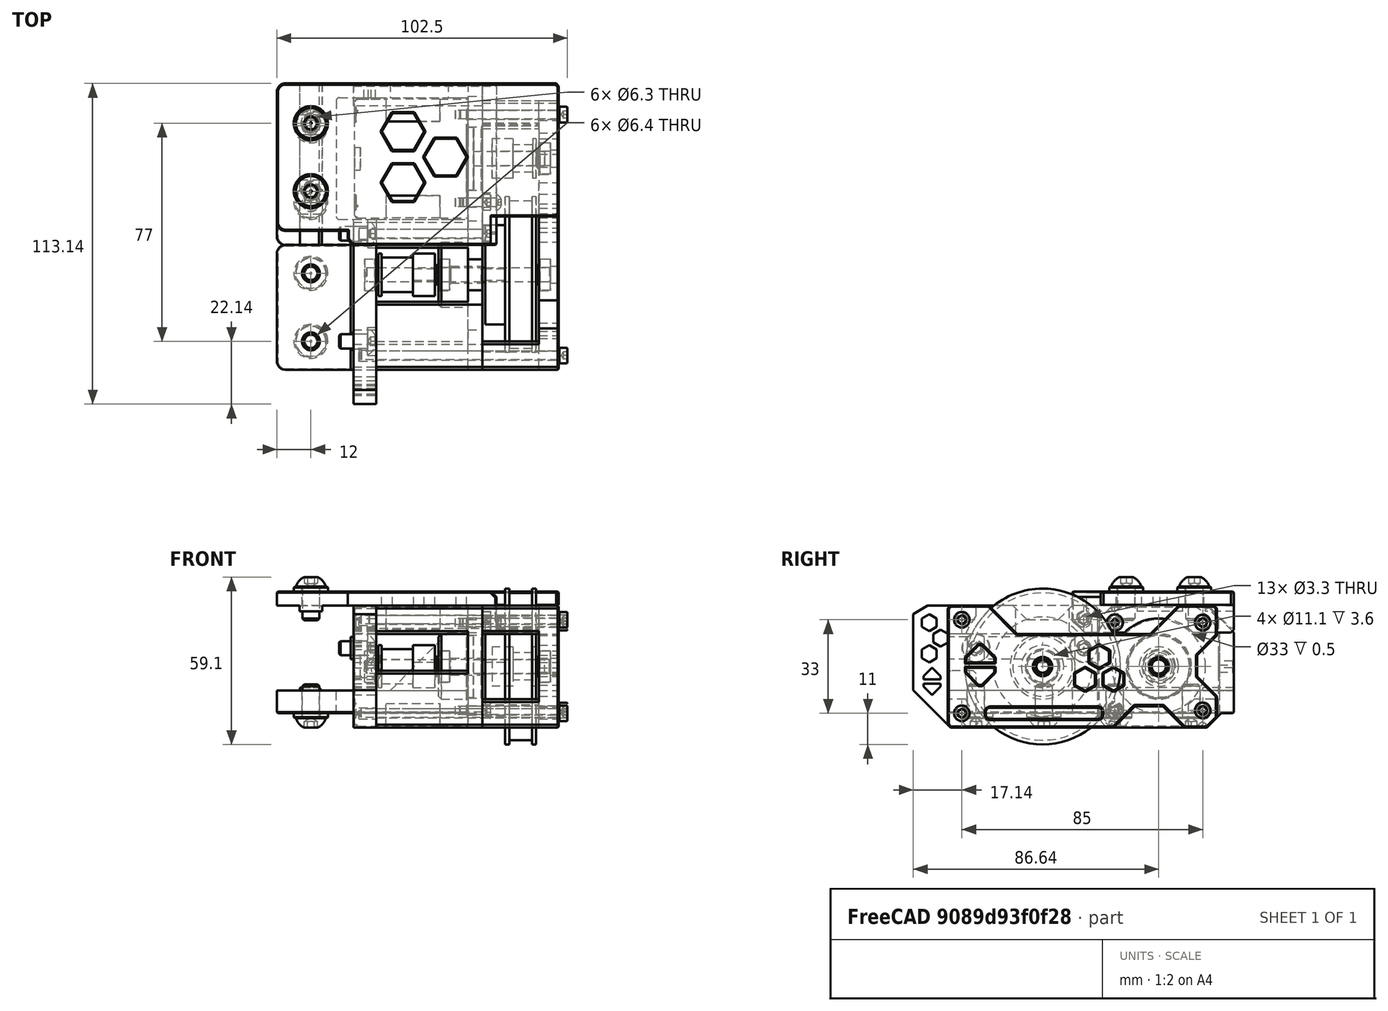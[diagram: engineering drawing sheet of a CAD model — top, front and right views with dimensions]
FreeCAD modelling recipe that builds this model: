
FCSTD DOCUMENT  (FreeCAD 0.19R24291 (Git))
Label: z-motor-left-assembly
License: Other
LicenseURL: GPL3
objects: Part::FeaturePython×21, Part::Feature×16, App::Part×1
note: 37 computed .brp shape members not serialized (recipe doc carries the construction recipe); baked Part::Feature solids carry a one-line shape summary decoded from their .brp

FEATURE [Part::Feature] Part__Mirroring014002  label="5mm-washer005"
  shape: bbox 0.5 x 6.9 x 6.9 mm, 4 faces (baked)
FEATURE [Part::Feature] Part__Mirroring002001  label="MR115ZZ006"
  shape: bbox 4 x 11 x 11 mm, 4 faces (baked)
FEATURE [Part::Feature] Part__Mirroring004001  label="20t-pulley001"
  shape: bbox 20 x 15 x 15 mm, 8 faces (baked)
FEATURE [Part::Feature] Part__Mirroring005001  label="MR115ZZ005"
  shape: bbox 4 x 11 x 11 mm, 4 faces (baked)
FEATURE [Part::Feature] Part__Mirroring007001  label="5mm-washer008"
  shape: bbox 0.5 x 6.9 x 6.9 mm, 4 faces (baked)
FEATURE [Part::Feature] Part__Mirroring008001  label="MR115ZZ007"
  shape: bbox 4 x 11 x 11 mm, 4 faces (baked)
FEATURE [Part::Feature] Part__Mirroring009001  label="motor-40mm001"
  shape: bbox 67 x 47 x 42 mm, 100 faces (baked)
FEATURE [Part::Feature] Part__Mirroring011001  label="5mm-washer006"
  shape: bbox 0.5 x 6.9 x 6.9 mm, 4 faces (baked)
FEATURE [Part::Feature] Part__Mirroring012001  label="5mm-washer007"
  shape: bbox 0.5 x 6.9 x 6.9 mm, 4 faces (baked)
FEATURE [Part::Feature] Part__Mirroring014001  label="16t-pulley001"
  shape: bbox 15.5 x 13.9 x 13.9 mm, 8 faces (baked)
FEATURE [Part::Feature] Part__Mirroring014004001  label="front-plate-type001"
  shape: bbox 27 x 95 x 43 mm, 156 faces (baked)
FEATURE [Part::Feature] Part__Mirroring014004003  label="back-plate-w-aligner001"
  shape: bbox 35 x 65.14 x 43 mm, 84 faces (baked)
FEATURE [Part::FeaturePython] Screw  label="M3x70-Screw"  # Fasteners workbench fastener (typed FeaturePython)
  Placement = pos=(72.5,-69.5,25) rot=(0,1,0;1.5708rad)
  baseObject = -> Part__Mirroring014004001 [Edge23]
  diameter = 4
  invert = true
  length = 10
  lengthCustom = 70
  matchOuter = true
  offset = 0
  thread = false
  type = 33
FEATURE [Part::FeaturePython] Screw001  label="M3x70-Screw001"  # Fasteners workbench fastener (typed FeaturePython)
  Placement = pos=(72.5,-69.5,-8) rot=(0,1,0;1.5708rad)
  baseObject = -> Part__Mirroring014004001 [Edge22]
  diameter = 4
  invert = true
  length = 10
  lengthCustom = 70
  matchOuter = true
  offset = 0
  thread = false
  type = 33
FEATURE [Part::FeaturePython] Screw002  label="M3x35-Screw"  # Fasteners workbench fastener (typed FeaturePython)
  Placement = pos=(72.5,15.5,24) rot=(0,1,0;1.5708rad)
  baseObject = -> Part__Mirroring014004001 [Edge24]
  diameter = 4
  invert = true
  length = 10
  lengthCustom = 35
  matchOuter = true
  offset = 0
  thread = false
  type = 33
FEATURE [Part::FeaturePython] Screw003  label="M3x35-Screw001"  # Fasteners workbench fastener (typed FeaturePython)
  Placement = pos=(72.5,15.5,-7) rot=(0,1,0;1.5708rad)
  baseObject = -> Part__Mirroring014004001 [Edge26]
  diameter = 4
  invert = true
  length = 10
  lengthCustom = 35
  matchOuter = true
  offset = 0
  thread = false
  type = 33
FEATURE [Part::FeaturePython] Screw004  label="M3x12-Screw"  # Fasteners workbench fastener (typed FeaturePython)
  Placement = pos=(50.5,-15.5,24) rot=(0,1,0;1.5708rad)
  diameter = 1
  invert = true
  length = 9
  lengthCustom = 12
  matchOuter = true
  offset = 0
  thread = false
  type = 39
FEATURE [Part::FeaturePython] Screw005  label="M3x8-Screw"  # Fasteners workbench fastener (typed FeaturePython)
  Placement = pos=(45.5,-15.5,-7) rot=(0,1,0;1.5708rad)
  diameter = 4
  invert = true
  length = 10
  lengthCustom = 8
  matchOuter = true
  offset = 0
  thread = false
  type = 33
FEATURE [Part::FeaturePython] Screw006  label="M5x10-Screw"  # Fasteners workbench fastener (typed FeaturePython)
  Placement = pos=(5,-64.5,15) rot=(0,1,0;1.5708rad)
  baseObject = -> Part__Mirroring014004003 [Edge90]
  diameter = 3
  invert = true
  length = 12
  lengthCustom = 10
  matchOuter = true
  offset = 0
  thread = false
  type = 39
FEATURE [Part::FeaturePython] Screw007  label="M5x10-Screw001"  # Fasteners workbench fastener (typed FeaturePython)
  Placement = pos=(5,-26.5,15) rot=(0,1,0;1.5708rad)
  baseObject = -> Part__Mirroring014004003 [Edge222]
  diameter = 3
  invert = true
  length = 12
  lengthCustom = 10
  matchOuter = true
  offset = 0
  thread = false
  type = 39
FEATURE [Part::FeaturePython] Washer  label="M6-Washer"  # Fasteners workbench fastener (typed FeaturePython)
  Placement = pos=(-15,-64.5,-8) rot=(1,0,0;3.14159rad)
  baseObject = -> Part__Mirroring014004003 [Edge185]
  diameter = 2
  invert = false
  matchOuter = true
  offset = 0
  type = 4
FEATURE [Part::FeaturePython] Washer001  label="M6-Washer001"  # Fasteners workbench fastener (typed FeaturePython)
  Placement = pos=(-15,-40.5,-8) rot=(1,0,0;3.14159rad)
  baseObject = -> Part__Mirroring014004003 [Edge183]
  diameter = 2
  invert = false
  matchOuter = true
  offset = 0
  type = 4
FEATURE [Part::FeaturePython] Washer002  label="M6-Washer006"  # Fasteners workbench fastener (typed FeaturePython)
  Placement = pos=(-15,-15.5,-8) rot=(1,0,0;3.14159rad)
  diameter = 2
  invert = false
  matchOuter = true
  offset = 0
  type = 4
FEATURE [Part::FeaturePython] Washer003  label="M6-Washer007"  # Fasteners workbench fastener (typed FeaturePython)
  Placement = pos=(-15,11.5,-8) rot=(1,0,0;3.14159rad)
  diameter = 2
  invert = false
  matchOuter = true
  offset = 0
  type = 4
FEATURE [Part::FeaturePython] Washer004  label="M6-Washer009"  # Fasteners workbench fastener (typed FeaturePython)
  Placement = pos=(-15,-11.5,35) rot=(0,0,1;0rad)
  diameter = 2
  invert = true
  matchOuter = true
  offset = 0
  type = 4
FEATURE [Part::FeaturePython] Washer005  label="M6-Washer008"  # Fasteners workbench fastener (typed FeaturePython)
  Placement = pos=(-15,12.5,35) rot=(0,0,1;0rad)
  diameter = 2
  invert = true
  matchOuter = true
  offset = 0
  type = 4
FEATURE [Part::FeaturePython] Screw008  label="M6x12-Screw"  # Fasteners workbench fastener (typed FeaturePython)
  Placement = pos=(-15,-11.5,36.8) rot=(0,0,1;0rad)
  baseObject = -> Washer004 [Edge1]
  diameter = 4
  invert = false
  length = 1
  lengthCustom = 12
  matchOuter = true
  offset = 0
  thread = false
  type = 39
FEATURE [Part::FeaturePython] Screw009  label="M6x12-Screw008"  # Fasteners workbench fastener (typed FeaturePython)
  Placement = pos=(-15,12.5,36.8) rot=(0,0,1;0rad)
  baseObject = -> Washer005 [Edge1]
  diameter = 4
  invert = false
  length = 1
  lengthCustom = 12
  matchOuter = true
  offset = 0
  thread = false
  type = 39
FEATURE [Part::FeaturePython] Screw010  label="M6x12-Screw006"  # Fasteners workbench fastener (typed FeaturePython)
  Placement = pos=(-15,11.5,-9.8) rot=(1,0,0;3.14159rad)
  baseObject = -> Washer003 [Edge1]
  diameter = 4
  invert = false
  length = 1
  lengthCustom = 12
  matchOuter = true
  offset = 0
  thread = false
  type = 39
FEATURE [Part::FeaturePython] Screw011  label="M6x12-Screw007"  # Fasteners workbench fastener (typed FeaturePython)
  Placement = pos=(-15,-15.5,-9.8) rot=(1,0,0;3.14159rad)
  baseObject = -> Washer002 [Edge1]
  diameter = 4
  invert = false
  length = 1
  lengthCustom = 12
  matchOuter = true
  offset = 0
  thread = false
  type = 39
FEATURE [Part::FeaturePython] Screw012  label="M6x12-Screw004"  # Fasteners workbench fastener (typed FeaturePython)
  Placement = pos=(-15,-40.5,-9.8) rot=(1,0,0;3.14159rad)
  baseObject = -> Washer001 [Edge1]
  diameter = 4
  invert = false
  length = 1
  lengthCustom = 12
  matchOuter = true
  offset = 0
  thread = false
  type = 39
FEATURE [Part::FeaturePython] Screw013  label="M6x12-Screw005"  # Fasteners workbench fastener (typed FeaturePython)
  Placement = pos=(-15,-64.5,-9.8) rot=(1,0,0;3.14159rad)
  baseObject = -> Washer [Edge1]
  diameter = 4
  invert = false
  length = 1
  lengthCustom = 12
  matchOuter = true
  offset = 0
  thread = false
  type = 39
FEATURE [Part::Feature] Part__Mirroring014004005  label="z-motor-plate-r004 (Mirror #1)001"
  shape: bbox 72.5 x 101 x 43 mm, 85 faces (baked)
FEATURE [Part::FeaturePython] Screw014  label="M3x40-Screw"  # Fasteners workbench fastener (typed FeaturePython)
  Placement = pos=(45.5,-26.5,25) rot=(0,1,0;1.5708rad)
  baseObject = -> Part__Mirroring014004005 [Edge95]
  diameter = 4
  invert = true
  length = 10
  lengthCustom = 40
  matchOuter = true
  offset = 0
  thread = false
  type = 33
FEATURE [Part::Feature] Cut001003001  label="80-t-mellow"
  Placement = pos=(64.5,-41,8.5) rot=(0,-1,0;1.5708rad)
  shape: bbox 18 x 55 x 55 mm, 10 faces (baked)
FEATURE [Part::Feature] Part__Mirroring014004008  label="Chamfer029006005001 (Mirror #1)001"
  shape: bbox 99.5 x 57 x 14.5 mm, 102 faces (baked)
FEATURE [Part::Feature] Body002  label="5x65-shaft"
  Placement = pos=(4.5,-41,8.5) rot=(0,0,1;0rad)
  shape: bbox 65 x 5 x 5 mm, 11 faces (baked)
FEATURE [App::Part] Part  label="z-motor-left"
  Group = -> [Part__Mirroring014002,Part__Mirroring002001,Part__Mirroring004001,Part__Mirroring005001,Part__Mirroring007001,Part__Mirroring008001,Part__Mirroring009001,Part__Mirroring011001,Part__Mirroring012001,Part__Mirroring014001,Part__Mirroring014004001,Part__Mirroring014004003,Screw002,Screw001,Screw003,Screw,Washer005,Washer004,Screw008,Screw009,Screw004,Washer002,Washer003,Screw010,Screw011,Screw005,+11 more]
  Origin = -> Origin
